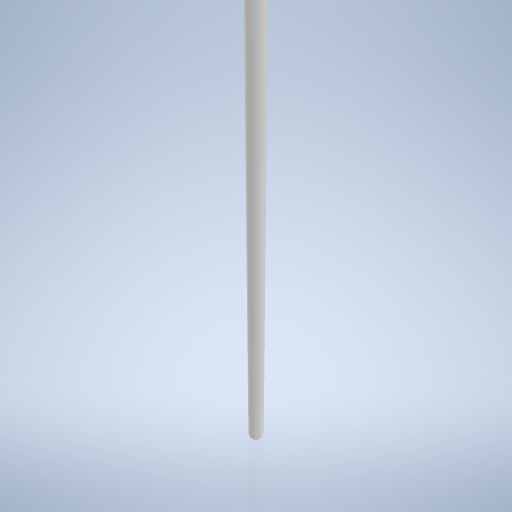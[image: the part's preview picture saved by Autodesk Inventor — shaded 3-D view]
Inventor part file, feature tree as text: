
AUTODESK INVENTOR PART (.ipt)
format: ipt  version: 2024.2 (Build 282272000, 272)  size: 243,712 bytes
history: native  units: mm
features: revolve x1, sketch x1
ambient origin geometry x8: Origin, YZ Plane, XZ Plane, XY Plane, X Axis, Y Axis, Z Axis, Center Point
bodies: Body1 (feature_tree)
feature tree (2):
  revolve  "Umdrehung1"
  sketch  "Skizze2"  dims[d3=1.0mm d4=58.0mm d5=2.0mm d6=90.0deg]
